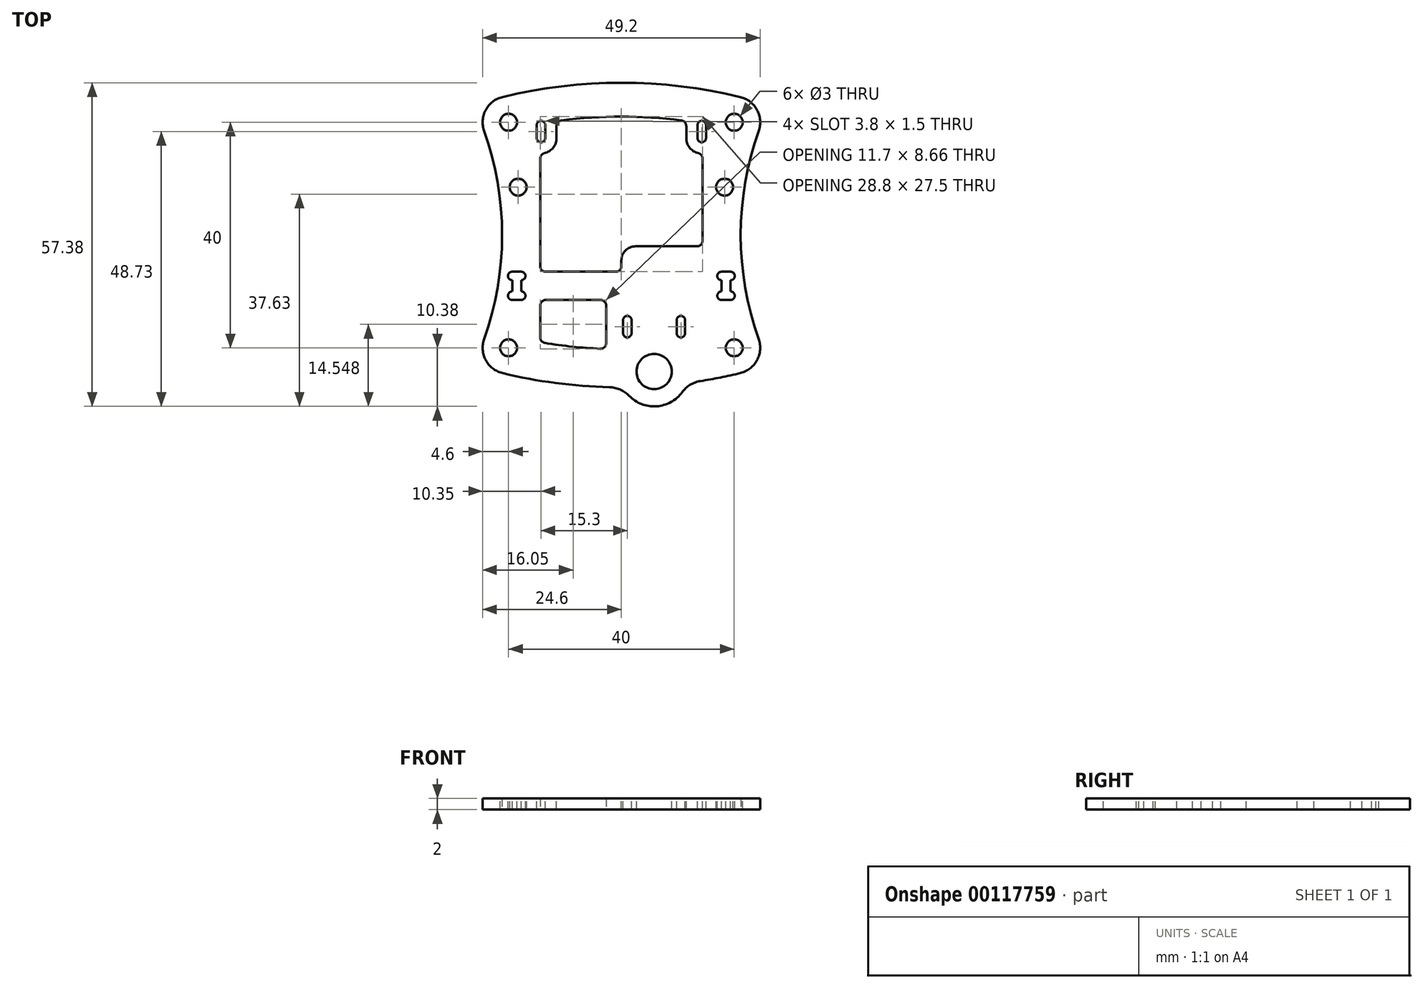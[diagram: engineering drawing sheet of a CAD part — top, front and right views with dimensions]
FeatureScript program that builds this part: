
annotation { "Feature Type Name" : "Feature", "Feature Type Description" : "" }
export const myFeature = defineFeature(function(context is Context, id is Id, definition is map)
    precondition{}
    {
        {
            var Q0;
            Q0=qCreatedBy(makeId("Top.planeOp"),FACE);
            var sketch = newSketch(context, id + "F0", { "sketchPlane" : qUnion([Q0])});
            skArc(sketch, "E0", {"start": v(-24.33, 18.46) * mm, "mid": v(-21.95, 9.37) * mm, "end": v(-21.15, 0) * mm});
            skLineSegment(sketch, "E1", {"start": v(-20, 0) * mm, "end": v(0, 0) * mm, "construction": true});
            skLineSegment(sketch, "E2", {"start": v(0, 0) * mm, "end": v(0, 20) * mm, "construction": true});
            skArc(sketch, "E3", {"start": v(-24.33, 18.46) * mm, "mid": v(-23.25, 23.25) * mm, "end": v(-18.46, 24.33) * mm});
            skArc(sketch, "E4", {"start": v(-18.46, 24.33) * mm, "mid": v(-9.37, 21.95) * mm, "end": v(0, 21.15) * mm});
            skPoint(sketch, "E4.centerSnap0", {"position": v(0, 10) * mm});
            skArc(sketch, "E5.MirrorCS", {"start": v(24.33, 18.46) * mm, "mid": v(23.25, 23.25) * mm, "end": v(18.46, 24.33) * mm});
            skArc(sketch, "E6.MirrorCS", {"start": v(24.33, 18.46) * mm, "mid": v(21.95, 9.37) * mm, "end": v(21.15, 0) * mm});
            skArc(sketch, "E7.MirrorCS", {"start": v(18.46, 24.33) * mm, "mid": v(9.37, 21.95) * mm, "end": v(0, 21.15) * mm});
            skPoint(sketch, "E8", {"position": v(-24.6, 20) * mm});
            skArc(sketch, "E9.MirrorCS", {"start": v(-24.33, -18.46) * mm, "mid": v(-21.95, -9.37) * mm, "end": v(-21.15, 0) * mm});
            skArc(sketch, "E10.MirrorCS", {"start": v(-24.33, -18.46) * mm, "mid": v(-23.25, -23.25) * mm, "end": v(-18.46, -24.33) * mm});
            skArc(sketch, "E11.MirrorCS", {"start": v(-18.46, -24.33) * mm, "mid": v(-9.37, -21.95) * mm, "end": v(0, -21.15) * mm});
            skArc(sketch, "E12.MirrorCS", {"start": v(24.33, -18.46) * mm, "mid": v(21.95, -9.37) * mm, "end": v(21.15, 0) * mm});
            skArc(sketch, "E13.MirrorCS", {"start": v(24.33, -18.46) * mm, "mid": v(23.25, -23.25) * mm, "end": v(18.46, -24.33) * mm});
            skArc(sketch, "E14.MirrorCS", {"start": v(18.46, -24.33) * mm, "mid": v(9.37, -21.95) * mm, "end": v(0, -21.15) * mm});
            skPoint(sketch, "E15.MirrorP", {"position": v(-24.6, -20) * mm});
            skSolve(sketch);
        }
        {
            var Q0;
            Q0 = qSketchRegion(id + "F0", true);
            extrude(context, id + "F1", {"entities" : qUnion([Q0]), "depth" : 2 * mm});
        }
        {
            var Q0;
            Q0=makeQuery(id+"F1.opExtrude","CAP_FACE",FACE,{"disambiguationData":[OSD([sQuery(id+"F0.wireOp",EDGE,"E0"),sQuery(id+"F0.wireOp",EDGE,"E3"),sQuery(id+"F0.wireOp",EDGE,"E4"),sQuery(id+"F0.wireOp",EDGE,"E5.MirrorCS"),sQuery(id+"F0.wireOp",EDGE,"E6.MirrorCS"),sQuery(id+"F0.wireOp",EDGE,"E7.MirrorCS"),sQuery(id+"F0.wireOp",EDGE,"E9.MirrorCS"),sQuery(id+"F0.wireOp",EDGE,"E11.MirrorCS"),sQuery(id+"F0.wireOp",EDGE,"E12.MirrorCS"),sQuery(id+"F0.wireOp",EDGE,"E13.MirrorCS"),sQuery(id+"F0.wireOp",EDGE,"E14.MirrorCS"),sQuery(id+"F0.wireOp",EDGE,"E10.MirrorCS")])],"isStart":false});
            var sketch = newSketch(context, id + "F2", { "sketchPlane" : qUnion([Q0])});
            skLineSegment(sketch, "E16", {"start": v(0, 0) * mm, "end": v(0, -65.87) * mm, "construction": true});
            skArc(sketch, "E17", {"start": v(-19.35, -6.5) * mm, "mid": v(-20.1, -7.25) * mm, "end": v(-19.35, -8) * mm});
            skLineSegment(sketch, "E18", {"start": v(-18.55, -6.5) * mm, "end": v(-18.55, -9) * mm, "construction": true});
            skLineSegment(sketch, "E19", {"start": v(-18.55, -9) * mm, "end": v(-19.35, -9) * mm, "construction": true});
            skLineSegment(sketch, "E20", {"start": v(-19.35, -6.5) * mm, "end": v(-18.55, -6.5) * mm});
            skLineSegment(sketch, "E21", {"start": v(-19.35, -8) * mm, "end": v(-19.35, -9) * mm});
            skLineSegment(sketch, "E22.MirrorCS", {"start": v(-19.35, -11.5) * mm, "end": v(-18.55, -11.5) * mm});
            skArc(sketch, "E23.MirrorCS", {"start": v(-19.35, -11.5) * mm, "mid": v(-20.1, -10.75) * mm, "end": v(-19.35, -10) * mm});
            skLineSegment(sketch, "E24.MirrorCS", {"start": v(-19.35, -10) * mm, "end": v(-19.35, -9) * mm});
            skArc(sketch, "E25.MirrorCS", {"start": v(-17.75, -11.5) * mm, "mid": v(-17, -10.75) * mm, "end": v(-17.75, -10) * mm});
            skLineSegment(sketch, "E26.MirrorCS", {"start": v(-17.75, -10) * mm, "end": v(-17.75, -9) * mm});
            skLineSegment(sketch, "E27.MirrorCS", {"start": v(-17.75, -8) * mm, "end": v(-17.75, -9) * mm});
            skArc(sketch, "E28.MirrorCS", {"start": v(-17.75, -6.5) * mm, "mid": v(-17, -7.25) * mm, "end": v(-17.75, -8) * mm});
            skLineSegment(sketch, "E29.MirrorCS", {"start": v(-17.75, -6.5) * mm, "end": v(-18.55, -6.5) * mm});
            skLineSegment(sketch, "E30.MirrorCS", {"start": v(-17.75, -11.5) * mm, "end": v(-18.55, -11.5) * mm});
            skArc(sketch, "E31.MirrorCS", {"start": v(19.35, -11.5) * mm, "mid": v(20.1, -10.75) * mm, "end": v(19.35, -10) * mm});
            skLineSegment(sketch, "E32.MirrorCS", {"start": v(19.35, -10) * mm, "end": v(19.35, -9) * mm});
            skLineSegment(sketch, "E33.MirrorCS", {"start": v(17.75, -8) * mm, "end": v(17.75, -9) * mm});
            skLineSegment(sketch, "E34.MirrorCS", {"start": v(19.35, -8) * mm, "end": v(19.35, -9) * mm});
            skArc(sketch, "E35.MirrorCS", {"start": v(17.75, -6.5) * mm, "mid": v(17, -7.25) * mm, "end": v(17.75, -8) * mm});
            skLineSegment(sketch, "E36.MirrorCS", {"start": v(17.75, -6.5) * mm, "end": v(18.55, -6.5) * mm});
            skLineSegment(sketch, "E37.MirrorCS", {"start": v(19.35, -6.5) * mm, "end": v(18.55, -6.5) * mm});
            skArc(sketch, "E38.MirrorCS", {"start": v(19.35, -6.5) * mm, "mid": v(20.1, -7.25) * mm, "end": v(19.35, -8) * mm});
            skLineSegment(sketch, "E39.MirrorCS", {"start": v(17.75, -10) * mm, "end": v(17.75, -9) * mm});
            skArc(sketch, "E40.MirrorCS", {"start": v(17.75, -11.5) * mm, "mid": v(17, -10.75) * mm, "end": v(17.75, -10) * mm});
            skLineSegment(sketch, "E41.MirrorCS", {"start": v(19.35, -11.5) * mm, "end": v(18.55, -11.5) * mm});
            skLineSegment(sketch, "E42.MirrorCS", {"start": v(17.75, -11.5) * mm, "end": v(18.55, -11.5) * mm});
            skSolve(sketch);
        }
        {
            var Q0;
            Q0 = qSketchRegion(id + "F2", true);
            extrude(context, id + "F3", {"entities" : qUnion([Q0]), "operationType" : NewBodyOperationType.REMOVE, "endBound" : BoundingType.THROUGH_ALL, "oppositeDirection" : true, "depth" : 25 * mm});
        }
        {
            var Q0;
            Q0=makeQuery(id+"F1.opExtrude","CAP_FACE",FACE,{"disambiguationData":[OSD([sQuery(id+"F0.wireOp",EDGE,"E0"),sQuery(id+"F0.wireOp",EDGE,"E3"),sQuery(id+"F0.wireOp",EDGE,"E4"),sQuery(id+"F0.wireOp",EDGE,"E5.MirrorCS"),sQuery(id+"F0.wireOp",EDGE,"E6.MirrorCS"),sQuery(id+"F0.wireOp",EDGE,"E7.MirrorCS"),sQuery(id+"F0.wireOp",EDGE,"E9.MirrorCS"),sQuery(id+"F0.wireOp",EDGE,"E11.MirrorCS"),sQuery(id+"F0.wireOp",EDGE,"E12.MirrorCS"),sQuery(id+"F0.wireOp",EDGE,"E13.MirrorCS"),sQuery(id+"F0.wireOp",EDGE,"E14.MirrorCS"),sQuery(id+"F0.wireOp",EDGE,"E10.MirrorCS")])],"isStart":false});
            var sketch = newSketch(context, id + "F4", { "sketchPlane" : qUnion([Q0])});
            skPoint(sketch, "E43", {"position": v(-20, 20) * mm});
            skPoint(sketch, "E44", {"position": v(20, 20) * mm});
            skPoint(sketch, "E45", {"position": v(20, -20) * mm});
            skPoint(sketch, "E46", {"position": v(-20, -20) * mm});
            skPoint(sketch, "E47", {"position": v(-18.3, 8.5) * mm});
            skPoint(sketch, "E48.MirrorP", {"position": v(18.3, 8.5) * mm});
            skSolve(sketch);
        }
        {
            var Q0;
            Q0=sQuery(id+"F4.wireOp",VERTEX,"E47");
            var Q1;
            Q1=sQuery(id+"F4.wireOp",VERTEX,"E43");
            var Q2;
            Q2=sQuery(id+"F4.wireOp",VERTEX,"E44");
            var Q3;
            Q3=sQuery(id+"F4.wireOp",VERTEX,"E48.MirrorP");
            var Q4;
            Q4=sQuery(id+"F4.wireOp",VERTEX,"E45");
            var Q5;
            Q5=sQuery(id+"F4.wireOp",VERTEX,"E46");
            var Q6;
            Q6=makeQuery(id+"F1.opExtrude","SWEPT_BODY",BODY,{"disambiguationData":[OSD([sQuery(id+"F0.wireOp",EDGE,"E0"),sQuery(id+"F0.wireOp",EDGE,"E3"),sQuery(id+"F0.wireOp",EDGE,"E4"),sQuery(id+"F0.wireOp",EDGE,"E5.MirrorCS"),sQuery(id+"F0.wireOp",EDGE,"E6.MirrorCS"),sQuery(id+"F0.wireOp",EDGE,"E7.MirrorCS"),sQuery(id+"F0.wireOp",EDGE,"E9.MirrorCS"),sQuery(id+"F0.wireOp",EDGE,"E11.MirrorCS"),sQuery(id+"F0.wireOp",EDGE,"E12.MirrorCS"),sQuery(id+"F0.wireOp",EDGE,"E13.MirrorCS"),sQuery(id+"F0.wireOp",EDGE,"E14.MirrorCS"),sQuery(id+"F0.wireOp",EDGE,"E10.MirrorCS")])]});
            hole(context, id + "F5", {"style" : HoleStyle.SIMPLE, "endStyle" : HoleEndStyle.THROUGH, "holeDiameter" : 3 * mm, "locations" : qUnion([Q0, Q1, Q2, Q3, Q4, Q5]), "scope" : qUnion([Q6]), "isTappedThrough" : true});
        }
        {
            var Q0;
            Q0=qCreatedBy(makeId("Top.planeOp"),FACE);
            var sketch = newSketch(context, id + "F6", { "sketchPlane" : qUnion([Q0])});
            skLineSegment(sketch, "E49", {"start": v(0, 0) * mm, "end": v(0, -30.33) * mm, "construction": true});
            skCircle(sketch, "E50", {"center": v(5.8, -24.2) * mm, "radius": 3.18 * mm});
            skLineSegment(sketch, "E51", {"start": v(-30.33, 18) * mm, "end": v(30.33, 18) * mm, "construction": true});
            skLineSegment(sketch, "E52", {"start": v(0, 0) * mm, "end": v(-30.33, 0) * mm, "construction": true});
            skLineSegment(sketch, "E53.bottom", {"start": v(-11, 25) * mm, "end": v(11, 25) * mm});
            skLineSegment(sketch, "E53.top", {"start": v(-11, -6) * mm, "end": v(11, -6) * mm});
            skLineSegment(sketch, "E53.left", {"start": v(-11, 25) * mm, "end": v(-11, -6) * mm});
            skLineSegment(sketch, "E53.right", {"start": v(11, 25) * mm, "end": v(11, -6) * mm});
            skLineSegment(sketch, "E54.bottom", {"start": v(-4, 25) * mm, "end": v(5.6, 25) * mm});
            skLineSegment(sketch, "E54.top", {"start": v(-4, 20) * mm, "end": v(5.6, 20) * mm});
            skLineSegment(sketch, "E54.left", {"start": v(-4, 25) * mm, "end": v(-4, 20) * mm});
            skLineSegment(sketch, "E54.right", {"start": v(5.6, 25) * mm, "end": v(5.6, 20) * mm});
            skLineSegment(sketch, "E55.bottom", {"start": v(1.25, -6) * mm, "end": v(10.35, -6) * mm});
            skLineSegment(sketch, "E55.top", {"start": v(1.25, -21.02) * mm, "end": v(10.35, -21.02) * mm});
            skLineSegment(sketch, "E55.left", {"start": v(1.25, -6) * mm, "end": v(1.25, -21.02) * mm});
            skLineSegment(sketch, "E55.right", {"start": v(10.35, -6) * mm, "end": v(10.35, -21.02) * mm});
            skLineSegment(sketch, "E56", {"start": v(5.8, -24.2) * mm, "end": v(5.8, -21.02) * mm, "construction": true});
            skPoint(sketch, "E56.endSnap0", {"position": v(5.8, -6) * mm});
            skLineSegment(sketch, "E57.bottom", {"start": v(-11, 0) * mm, "end": v(11, 0) * mm});
            skLineSegment(sketch, "E57.top", {"start": v(-11, 19.5) * mm, "end": v(11, 19.5) * mm});
            skLineSegment(sketch, "E57.left", {"start": v(-11, 0) * mm, "end": v(-11, 19.5) * mm});
            skLineSegment(sketch, "E57.right", {"start": v(11, 0) * mm, "end": v(11, 19.5) * mm});
            skSolve(sketch);
        }
        {
            var Q0;
            Q0=qCreatedBy(makeId("Top.planeOp"),FACE);
            var sketch = newSketch(context, id + "F7", { "sketchPlane" : qUnion([Q0])});
            skLineSegment(sketch, "E58", {"start": v(0, 0) * mm, "end": v(0, 27) * mm, "construction": true});
            skArc(sketch, "E59", {"start": v(0, 27) * mm, "mid": v(-10.62, 26.37) * mm, "end": v(-21.09, 24.47) * mm});
            skLineSegment(sketch, "E60", {"start": v(0, 27) * mm, "end": v(-20.39, 27) * mm, "construction": true});
            skArc(sketch, "E61", {"start": v(-21.09, 24.47) * mm, "mid": v(-19.76, 24.6) * mm, "end": v(-18.46, 24.33) * mm});
            skArc(sketch, "E62", {"start": v(-18.46, 24.33) * mm, "mid": v(-9.37, 21.95) * mm, "end": v(0, 21.15) * mm});
            skArc(sketch, "E63.MirrorCS", {"start": v(18.46, 24.33) * mm, "mid": v(9.37, 21.95) * mm, "end": v(0, 21.15) * mm});
            skArc(sketch, "E64.MirrorCS", {"start": v(21.09, 24.47) * mm, "mid": v(19.76, 24.6) * mm, "end": v(18.46, 24.33) * mm});
            skArc(sketch, "E65.MirrorCS", {"start": v(0, 27) * mm, "mid": v(10.62, 26.37) * mm, "end": v(21.09, 24.47) * mm});
            skSolve(sketch);
        }
        {
            var Q0;
            Q0 = qSketchRegion(id + "F7", true);
            var Q1;
            Q1=makeQuery(id+"F1.opExtrude","CAP_FACE",FACE,{"disambiguationData":[OSD([sQuery(id+"F0.wireOp",EDGE,"E0"),sQuery(id+"F0.wireOp",EDGE,"E3"),sQuery(id+"F0.wireOp",EDGE,"E4"),sQuery(id+"F0.wireOp",EDGE,"E5.MirrorCS"),sQuery(id+"F0.wireOp",EDGE,"E6.MirrorCS"),sQuery(id+"F0.wireOp",EDGE,"E7.MirrorCS"),sQuery(id+"F0.wireOp",EDGE,"E9.MirrorCS"),sQuery(id+"F0.wireOp",EDGE,"E11.MirrorCS"),sQuery(id+"F0.wireOp",EDGE,"E12.MirrorCS"),sQuery(id+"F0.wireOp",EDGE,"E13.MirrorCS"),sQuery(id+"F0.wireOp",EDGE,"E14.MirrorCS"),sQuery(id+"F0.wireOp",EDGE,"E10.MirrorCS")])],"isStart":false});
            extrude(context, id + "F8", {"entities" : qUnion([Q0]), "operationType" : NewBodyOperationType.ADD, "endBound" : BoundingType.UP_TO_SURFACE, "endBoundEntityFace" : qUnion([Q1]), "depth" : 25 * mm});
        }
        {
            var Q0;
            Q0=qCreatedBy(makeId("Top.planeOp"),FACE);
            var sketch = newSketch(context, id + "F9", { "sketchPlane" : qUnion([Q0])});
            skLineSegment(sketch, "E66", {"start": v(0, 0) * mm, "end": v(30.86, 0) * mm, "construction": true});
            skArc(sketch, "E67", {"start": v(21.09, -24.47) * mm, "mid": v(16.38, -25.48) * mm, "end": v(11.63, -26.24) * mm});
            skLineSegment(sketch, "E68", {"start": v(0, -27) * mm, "end": v(0, 0) * mm, "construction": true});
            skLineSegment(sketch, "E69", {"start": v(0, -27) * mm, "end": v(19.98, -27) * mm, "construction": true});
            skArc(sketch, "E70.MirrorCS", {"start": v(-21.09, -24.47) * mm, "mid": v(-10.47, -26.38) * mm, "end": v(0.3, -27) * mm});
            skArc(sketch, "E71", {"start": v(0.3, -27) * mm, "mid": v(6.21, -30.36) * mm, "end": v(11.63, -26.24) * mm});
            skArc(sketch, "E72", {"start": v(0, -21.15) * mm, "mid": v(9.37, -21.95) * mm, "end": v(18.46, -24.33) * mm});
            skArc(sketch, "E73", {"start": v(21.09, -24.47) * mm, "mid": v(19.76, -24.6) * mm, "end": v(18.46, -24.33) * mm});
            skArc(sketch, "E74.MirrorCS", {"start": v(-21.09, -24.47) * mm, "mid": v(-19.76, -24.6) * mm, "end": v(-18.46, -24.33) * mm});
            skArc(sketch, "E75.MirrorCS", {"start": v(0, -21.15) * mm, "mid": v(-9.37, -21.95) * mm, "end": v(-18.46, -24.33) * mm});
            skPoint(sketch, "E76.orphan", {"position": v(0, -27) * mm});
            skSolve(sketch);
        }
        {
            var Q0;
            Q0 = qSketchRegion(id + "F9", true);
            var Q1;
            {var subQ0=sQuery(id+"F0.wireOp",EDGE,"E10.MirrorCS");var subQ1=sQuery(id+"F0.wireOp",EDGE,"E14.MirrorCS");var subQ2=sQuery(id+"F0.wireOp",EDGE,"E13.MirrorCS");var subQ3=sQuery(id+"F0.wireOp",EDGE,"E12.MirrorCS");var subQ4=sQuery(id+"F0.wireOp",EDGE,"E11.MirrorCS");var subQ5=sQuery(id+"F0.wireOp",EDGE,"E9.MirrorCS");var subQ6=sQuery(id+"F0.wireOp",EDGE,"E7.MirrorCS");var subQ7=sQuery(id+"F0.wireOp",EDGE,"E6.MirrorCS");var subQ8=sQuery(id+"F0.wireOp",EDGE,"E5.MirrorCS");var subQ9=sQuery(id+"F0.wireOp",EDGE,"E4");var subQ10=sQuery(id+"F0.wireOp",EDGE,"E3");var subQ11=sQuery(id+"F0.wireOp",EDGE,"E0");Q1=makeQuery(id+"F8.boolean.opBoolean","MERGE",FACE,{"derivedFrom":[makeQuery(id+"F1.opExtrude","CAP_FACE",FACE,{"disambiguationData":[OSD([subQ11,subQ10,subQ9,subQ8,subQ7,subQ6,subQ5,subQ4,subQ3,subQ2,subQ1,subQ0])],"isStart":false}),makeQuery(id+"F8.opExtrude","CAP_FACE",FACE,{"disambiguationData":[OSD([subQ11,subQ10,subQ9,subQ8,subQ7,subQ6,subQ5,subQ4,subQ3,subQ2,subQ1,subQ0])],"isStart":false})]});}
            extrude(context, id + "F10", {"entities" : qUnion([Q0]), "operationType" : NewBodyOperationType.ADD, "endBound" : BoundingType.UP_TO_SURFACE, "endBoundEntityFace" : qUnion([Q1]), "depth" : 25 * mm});
        }
        {
            var Q0;
            Q0=makeQuery(id+"F10.opExtrude","SWEPT_EDGE",EDGE,{"disambiguationData":[OSD([sQuery(id+"F9.wireOp",EDGE,"E70.MirrorCS"),sQuery(id+"F9.wireOp",EDGE,"E71")])]});
            var Q1;
            Q1=makeQuery(id+"F10.opExtrude","SWEPT_EDGE",EDGE,{"disambiguationData":[OSD([sQuery(id+"F9.wireOp",EDGE,"E67"),sQuery(id+"F9.wireOp",EDGE,"E71")])]});
            fillet(context, id + "F11", {"entities" : qUnion([Q0, Q1]), "radius" : 5 * mm, "tangentPropagation" : true, "allowEdgeOverflow" : false});
        }
        {
            var Q0;
            {var subQ0=sQuery(id+"F0.wireOp",EDGE,"E10.MirrorCS");var subQ1=sQuery(id+"F0.wireOp",EDGE,"E14.MirrorCS");var subQ2=sQuery(id+"F0.wireOp",EDGE,"E13.MirrorCS");var subQ3=sQuery(id+"F0.wireOp",EDGE,"E12.MirrorCS");var subQ4=sQuery(id+"F0.wireOp",EDGE,"E11.MirrorCS");var subQ5=sQuery(id+"F0.wireOp",EDGE,"E9.MirrorCS");var subQ6=sQuery(id+"F0.wireOp",EDGE,"E7.MirrorCS");var subQ7=sQuery(id+"F0.wireOp",EDGE,"E6.MirrorCS");var subQ8=sQuery(id+"F0.wireOp",EDGE,"E5.MirrorCS");var subQ9=sQuery(id+"F0.wireOp",EDGE,"E4");var subQ10=sQuery(id+"F0.wireOp",EDGE,"E3");var subQ11=sQuery(id+"F0.wireOp",EDGE,"E0");Q0=makeQuery(id+"F10.boolean.opBoolean","MERGE",FACE,{"derivedFrom":[makeQuery(id+"F8.boolean.opBoolean","MERGE",FACE,{"derivedFrom":[makeQuery(id+"F1.opExtrude","CAP_FACE",FACE,{"disambiguationData":[OSD([subQ11,subQ10,subQ9,subQ8,subQ7,subQ6,subQ5,subQ4,subQ3,subQ2,subQ1,subQ0])],"isStart":false}),makeQuery(id+"F8.opExtrude","CAP_FACE",FACE,{"disambiguationData":[OSD([subQ11,subQ10,subQ9,subQ8,subQ7,subQ6,subQ5,subQ4,subQ3,subQ2,subQ1,subQ0])],"isStart":false})]}),makeQuery(id+"F10.opExtrude","CAP_FACE",FACE,{"disambiguationData":[OSD([subQ11,subQ10,subQ9,subQ8,subQ7,subQ6,subQ5,subQ4,subQ3,subQ2,subQ1,subQ0])],"isStart":false})]});}
            var sketch = newSketch(context, id + "F12", { "sketchPlane" : qUnion([Q0])});
            skLineSegment(sketch, "E77", {"start": v(5.8, 3.6) * mm, "end": v(5.8, -24.2) * mm, "construction": true});
            skLineSegment(sketch, "E78", {"start": v(0, 0) * mm, "end": v(0, 29.06) * mm, "construction": true});
            skPoint(sketch, "E78.endSnap0", {"position": v(0, 27) * mm});
            skLineSegment(sketch, "E79.left", {"start": v(9.8, -15.1) * mm, "end": v(9.8, -17.4) * mm});
            skLineSegment(sketch, "E79.right", {"start": v(11.3, -15.1) * mm, "end": v(11.3, -17.4) * mm});
            skArc(sketch, "E80", {"start": v(11.3, -15.1) * mm, "mid": v(10.55, -14.35) * mm, "end": v(9.8, -15.1) * mm});
            skArc(sketch, "E81", {"start": v(9.8, -17.4) * mm, "mid": v(10.55, -18.15) * mm, "end": v(11.3, -17.4) * mm});
            skLineSegment(sketch, "E82", {"start": v(10.55, -17.4) * mm, "end": v(10.55, -15.1) * mm});
            skPoint(sketch, "E83", {"position": v(10.55, -16.25) * mm});
            skLineSegment(sketch, "E84.MirrorCS", {"start": v(0.3, -15.1) * mm, "end": v(0.3, -17.4) * mm});
            skArc(sketch, "E85.MirrorCS", {"start": v(0.3, -15.1) * mm, "mid": v(1.05, -14.35) * mm, "end": v(1.8, -15.1) * mm});
            skLineSegment(sketch, "E86.MirrorCS", {"start": v(1.8, -15.1) * mm, "end": v(1.8, -17.4) * mm});
            skArc(sketch, "E87.MirrorCS", {"start": v(1.8, -17.4) * mm, "mid": v(1.05, -18.15) * mm, "end": v(0.3, -17.4) * mm});
            skLineSegment(sketch, "E88.left", {"start": v(13.5, 19.5) * mm, "end": v(13.5, 17.2) * mm});
            skLineSegment(sketch, "E88.right", {"start": v(15, 19.5) * mm, "end": v(15, 17.2) * mm});
            skArc(sketch, "E89", {"start": v(15, 19.5) * mm, "mid": v(14.25, 20.25) * mm, "end": v(13.5, 19.5) * mm});
            skArc(sketch, "E90", {"start": v(13.5, 17.2) * mm, "mid": v(14.25, 16.45) * mm, "end": v(15, 17.2) * mm});
            skArc(sketch, "E91.MirrorCS", {"start": v(-15, 19.5) * mm, "mid": v(-14.25, 20.25) * mm, "end": v(-13.5, 19.5) * mm});
            skLineSegment(sketch, "E92.MirrorCS", {"start": v(-13.5, 19.5) * mm, "end": v(-13.5, 17.2) * mm});
            skLineSegment(sketch, "E93.MirrorCS", {"start": v(-15, 19.5) * mm, "end": v(-15, 17.2) * mm});
            skArc(sketch, "E94.MirrorCS", {"start": v(-13.5, 17.2) * mm, "mid": v(-14.25, 16.45) * mm, "end": v(-15, 17.2) * mm});
            skSolve(sketch);
        }
        {
            var Q0;
            Q0 = qSketchRegion(id + "F12", true);
            extrude(context, id + "F13", {"entities" : qUnion([Q0]), "operationType" : NewBodyOperationType.REMOVE, "endBound" : BoundingType.THROUGH_ALL, "oppositeDirection" : true, "depth" : 25 * mm});
        }
        {
            var Q0;
            {var subQ0=sQuery(id+"F0.wireOp",EDGE,"E10.MirrorCS");var subQ1=sQuery(id+"F0.wireOp",EDGE,"E14.MirrorCS");var subQ2=sQuery(id+"F0.wireOp",EDGE,"E13.MirrorCS");var subQ3=sQuery(id+"F0.wireOp",EDGE,"E12.MirrorCS");var subQ4=sQuery(id+"F0.wireOp",EDGE,"E11.MirrorCS");var subQ5=sQuery(id+"F0.wireOp",EDGE,"E9.MirrorCS");var subQ6=sQuery(id+"F0.wireOp",EDGE,"E7.MirrorCS");var subQ7=sQuery(id+"F0.wireOp",EDGE,"E6.MirrorCS");var subQ8=sQuery(id+"F0.wireOp",EDGE,"E5.MirrorCS");var subQ9=sQuery(id+"F0.wireOp",EDGE,"E4");var subQ10=sQuery(id+"F0.wireOp",EDGE,"E3");var subQ11=sQuery(id+"F0.wireOp",EDGE,"E0");Q0=makeQuery(id+"F10.boolean.opBoolean","MERGE",FACE,{"derivedFrom":[makeQuery(id+"F8.boolean.opBoolean","MERGE",FACE,{"derivedFrom":[makeQuery(id+"F1.opExtrude","CAP_FACE",FACE,{"disambiguationData":[OSD([subQ11,subQ10,subQ9,subQ8,subQ7,subQ6,subQ5,subQ4,subQ3,subQ2,subQ1,subQ0])],"isStart":false}),makeQuery(id+"F8.opExtrude","CAP_FACE",FACE,{"disambiguationData":[OSD([subQ11,subQ10,subQ9,subQ8,subQ7,subQ6,subQ5,subQ4,subQ3,subQ2,subQ1,subQ0])],"isStart":false})]}),makeQuery(id+"F10.opExtrude","CAP_FACE",FACE,{"disambiguationData":[OSD([subQ11,subQ10,subQ9,subQ8,subQ7,subQ6,subQ5,subQ4,subQ3,subQ2,subQ1,subQ0])],"isStart":false})]});}
            var sketch = newSketch(context, id + "F14", { "sketchPlane" : qUnion([Q0])});
            skCircle(sketch, "E95", {"center": v(5.8, -24.2) * mm, "radius": 3.12 * mm});
            skSolve(sketch);
        }
        {
            var Q0;
            Q0 = qSketchRegion(id + "F14", true);
            extrude(context, id + "F15", {"entities" : qUnion([Q0]), "operationType" : NewBodyOperationType.REMOVE, "endBound" : BoundingType.THROUGH_ALL, "oppositeDirection" : true, "depth" : 25 * mm});
        }
        {
            var Q0;
            {var subQ0=sQuery(id+"F0.wireOp",EDGE,"E10.MirrorCS");var subQ1=sQuery(id+"F0.wireOp",EDGE,"E14.MirrorCS");var subQ2=sQuery(id+"F0.wireOp",EDGE,"E13.MirrorCS");var subQ3=sQuery(id+"F0.wireOp",EDGE,"E12.MirrorCS");var subQ4=sQuery(id+"F0.wireOp",EDGE,"E11.MirrorCS");var subQ5=sQuery(id+"F0.wireOp",EDGE,"E9.MirrorCS");var subQ6=sQuery(id+"F0.wireOp",EDGE,"E7.MirrorCS");var subQ7=sQuery(id+"F0.wireOp",EDGE,"E6.MirrorCS");var subQ8=sQuery(id+"F0.wireOp",EDGE,"E5.MirrorCS");var subQ9=sQuery(id+"F0.wireOp",EDGE,"E4");var subQ10=sQuery(id+"F0.wireOp",EDGE,"E3");var subQ11=sQuery(id+"F0.wireOp",EDGE,"E0");Q0=makeQuery(id+"F10.boolean.opBoolean","MERGE",FACE,{"derivedFrom":[makeQuery(id+"F8.boolean.opBoolean","MERGE",FACE,{"derivedFrom":[makeQuery(id+"F1.opExtrude","CAP_FACE",FACE,{"disambiguationData":[OSD([subQ11,subQ10,subQ9,subQ8,subQ7,subQ6,subQ5,subQ4,subQ3,subQ2,subQ1,subQ0])],"isStart":false}),makeQuery(id+"F8.opExtrude","CAP_FACE",FACE,{"disambiguationData":[OSD([subQ11,subQ10,subQ9,subQ8,subQ7,subQ6,subQ5,subQ4,subQ3,subQ2,subQ1,subQ0])],"isStart":false})]}),makeQuery(id+"F10.opExtrude","CAP_FACE",FACE,{"disambiguationData":[OSD([subQ11,subQ10,subQ9,subQ8,subQ7,subQ6,subQ5,subQ4,subQ3,subQ2,subQ1,subQ0])],"isStart":false})]});}
            var sketch = newSketch(context, id + "F16", { "sketchPlane" : qUnion([Q0])});
            skPoint(sketch, "E96", {"position": v(0, 27) * mm});
            skLineSegment(sketch, "E97", {"start": v(-14.4, 14.45) * mm, "end": v(-14.4, -6.5) * mm});
            skPoint(sketch, "E98", {"position": v(-21.15, 0) * mm});
            skLineSegment(sketch, "E99", {"start": v(14.4, 14.45) * mm, "end": v(14.4, -2) * mm});
            skPoint(sketch, "E100", {"position": v(21.15, 0) * mm});
            skArc(sketch, "E101", {"start": v(-11.5, 20.2) * mm, "mid": v(0, 21) * mm, "end": v(11.5, 20.2) * mm});
            skLineSegment(sketch, "E102", {"start": v(-2.7, -20.2) * mm, "end": v(-2.7, -11.5) * mm});
            skLineSegment(sketch, "E103", {"start": v(0, -2) * mm, "end": v(14.4, -2) * mm});
            skLineSegment(sketch, "E104", {"start": v(-11.5, 17.2) * mm, "end": v(-11.5, 20.2) * mm});
            skPoint(sketch, "E105", {"position": v(-14.25, 17.2) * mm});
            skArc(sketch, "E106", {"start": v(-11.5, 17.2) * mm, "mid": v(-12.36, 15.2) * mm, "end": v(-14.4, 14.45) * mm});
            skLineSegment(sketch, "E107", {"start": v(0, 0) * mm, "end": v(0, 21) * mm, "construction": true});
            skPoint(sketch, "E108", {"position": v(-14.25, 16.45) * mm});
            skArc(sketch, "E109.MirrorCS", {"start": v(11.5, 17.2) * mm, "mid": v(12.36, 15.2) * mm, "end": v(14.4, 14.45) * mm});
            skLineSegment(sketch, "E110.MirrorCS", {"start": v(11.5, 17.2) * mm, "end": v(11.5, 20.2) * mm});
            skArc(sketch, "E111", {"start": v(-14.4, -18.98) * mm, "mid": v(-8.57, -19.8) * mm, "end": v(-2.7, -20.2) * mm});
            skLineSegment(sketch, "E112", {"start": v(-2.7, -11.5) * mm, "end": v(-14.4, -11.5) * mm});
            skLineSegment(sketch, "E113", {"start": v(-14.4, -6.5) * mm, "end": v(0, -6.5) * mm});
            skLineSegment(sketch, "E114.trimOffspring", {"start": v(0, -6.5) * mm, "end": v(0, -2) * mm});
            skLineSegment(sketch, "E115.trimOffspring", {"start": v(-14.4, -11.5) * mm, "end": v(-14.4, -18.98) * mm});
            skLineSegment(sketch, "E116", {"start": v(5.8, -24.2) * mm, "end": v(5.8, -21.07) * mm, "construction": true});
            skSolve(sketch);
        }
        {
            var Q0;
            Q0 = qSketchRegion(id + "F16", true);
            extrude(context, id + "F17", {"entities" : qUnion([Q0]), "operationType" : NewBodyOperationType.REMOVE, "endBound" : BoundingType.THROUGH_ALL, "oppositeDirection" : true, "depth" : 25 * mm});
        }
        {
            var Q0;
            Q0=makeQuery(id+"F17.boolean.opBoolean","COPY",EDGE,{"derivedFrom":makeQuery(id+"F17.opExtrude","SWEPT_EDGE",EDGE,{"disambiguationData":[OSD([sQuery(id+"F16.wireOp",EDGE,"E102"),sQuery(id+"F16.wireOp",EDGE,"E112")])]})});
            var Q1;
            Q1=makeQuery(id+"F17.boolean.opBoolean","COPY",EDGE,{"derivedFrom":makeQuery(id+"F17.opExtrude","SWEPT_EDGE",EDGE,{"disambiguationData":[OSD([sQuery(id+"F16.wireOp",EDGE,"w48rfDKU-Ewvb-xwgp-HWHa-MmorG8pKUdSB.bottom"),sQuery(id+"F16.wireOp",EDGE,"w48rfDKU-Ewvb-xwgp-HWHa-MmorG8pKUdSB.right")])]})});
            var Q2;
            Q2=makeQuery(id+"F17.boolean.opBoolean","COPY",EDGE,{"derivedFrom":makeQuery(id+"F17.opExtrude","SWEPT_EDGE",EDGE,{"disambiguationData":[OSD([sQuery(id+"F16.wireOp",EDGE,"E112"),sQuery(id+"F16.wireOp",EDGE,"E115.trimOffspring")])]})});
            var Q3;
            Q3=makeQuery(id+"F17.boolean.opBoolean","COPY",EDGE,{"derivedFrom":makeQuery(id+"F17.opExtrude","SWEPT_EDGE",EDGE,{"disambiguationData":[OSD([sQuery(id+"F16.wireOp",EDGE,"E111"),sQuery(id+"F16.wireOp",EDGE,"E115.trimOffspring")])]})});
            var Q4;
            Q4=makeQuery(id+"F17.boolean.opBoolean","COPY",EDGE,{"derivedFrom":makeQuery(id+"F17.opExtrude","SWEPT_EDGE",EDGE,{"disambiguationData":[OSD([sQuery(id+"F16.wireOp",EDGE,"w48rfDKU-Ewvb-xwgp-HWHa-MmorG8pKUdSB.top"),sQuery(id+"F16.wireOp",EDGE,"w48rfDKU-Ewvb-xwgp-HWHa-MmorG8pKUdSB.left")])]})});
            var Q5;
            Q5=makeQuery(id+"F17.boolean.opBoolean","COPY",EDGE,{"derivedFrom":makeQuery(id+"F17.opExtrude","SWEPT_EDGE",EDGE,{"disambiguationData":[OSD([sQuery(id+"F16.wireOp",EDGE,"w48rfDKU-Ewvb-xwgp-HWHa-MmorG8pKUdSB.top"),sQuery(id+"F16.wireOp",EDGE,"w48rfDKU-Ewvb-xwgp-HWHa-MmorG8pKUdSB.right")])]})});
            var Q6;
            Q6=makeQuery(id+"F17.boolean.opBoolean","COPY",EDGE,{"derivedFrom":makeQuery(id+"F17.opExtrude","SWEPT_EDGE",EDGE,{"disambiguationData":[OSD([sQuery(id+"F16.wireOp",EDGE,"E102"),sQuery(id+"F16.wireOp",EDGE,"E111")])]})});
            var Q7;
            Q7=makeQuery(id+"F17.boolean.opBoolean","COPY",EDGE,{"derivedFrom":makeQuery(id+"F17.opExtrude","SWEPT_EDGE",EDGE,{"disambiguationData":[OSD([sQuery(id+"F16.wireOp",EDGE,"w48rfDKU-Ewvb-xwgp-HWHa-MmorG8pKUdSB.bottom"),sQuery(id+"F16.wireOp",EDGE,"w48rfDKU-Ewvb-xwgp-HWHa-MmorG8pKUdSB.left")])]})});
            var Q8;
            Q8=makeQuery(id+"F17.boolean.opBoolean","COPY",EDGE,{"derivedFrom":makeQuery(id+"F17.opExtrude","SWEPT_EDGE",EDGE,{"disambiguationData":[OSD([sQuery(id+"F16.wireOp",EDGE,"E101"),sQuery(id+"F16.wireOp",EDGE,"E110.MirrorCS")])]})});
            var Q9;
            Q9=makeQuery(id+"F17.boolean.opBoolean","COPY",EDGE,{"derivedFrom":makeQuery(id+"F17.opExtrude","SWEPT_EDGE",EDGE,{"disambiguationData":[OSD([sQuery(id+"F16.wireOp",EDGE,"E99"),sQuery(id+"F16.wireOp",EDGE,"242761ee-4380-49e1-bb36-9e82733fe9be0.MirrorCS")])]})});
            var Q10;
            Q10=makeQuery(id+"F17.boolean.opBoolean","COPY",EDGE,{"derivedFrom":makeQuery(id+"F17.opExtrude","SWEPT_EDGE",EDGE,{"disambiguationData":[OSD([sQuery(id+"F16.wireOp",EDGE,"E97"),sQuery(id+"F16.wireOp",EDGE,"YmPafNJ4-ENFf-a7qC-zsAM-NMp7mHHc5WH0")])]})});
            var Q11;
            Q11=makeQuery(id+"F17.boolean.opBoolean","COPY",EDGE,{"derivedFrom":makeQuery(id+"F17.opExtrude","SWEPT_EDGE",EDGE,{"disambiguationData":[OSD([sQuery(id+"F16.wireOp",EDGE,"E101"),sQuery(id+"F16.wireOp",EDGE,"E104")])]})});
            var Q12;
            Q12=makeQuery(id+"F17.boolean.opBoolean","COPY",EDGE,{"derivedFrom":makeQuery(id+"F17.opExtrude","SWEPT_EDGE",EDGE,{"disambiguationData":[OSD([sQuery(id+"F16.wireOp",EDGE,"E97"),sQuery(id+"F16.wireOp",EDGE,"E113")])]})});
            var Q13;
            Q13=makeQuery(id+"F17.boolean.opBoolean","COPY",EDGE,{"derivedFrom":makeQuery(id+"F17.opExtrude","SWEPT_EDGE",EDGE,{"disambiguationData":[OSD([sQuery(id+"F16.wireOp",EDGE,"E99"),sQuery(id+"F16.wireOp",EDGE,"E103")])]})});
            var Q14;
            Q14=makeQuery(id+"F17.boolean.opBoolean","COPY",EDGE,{"derivedFrom":makeQuery(id+"F17.opExtrude","SWEPT_EDGE",EDGE,{"disambiguationData":[OSD([sQuery(id+"F16.wireOp",EDGE,"E113"),sQuery(id+"F16.wireOp",EDGE,"E114.trimOffspring")])]})});
            fillet(context, id + "F18", {"entities" : qUnion([Q0, Q1, Q2, Q3, Q4, Q5, Q6, Q7, Q8, Q9, Q10, Q11, Q12, Q13, Q14]), "radius" : 1 * mm, "tangentPropagation" : true, "allowEdgeOverflow" : false});
        }
        {
            var Q0;
            Q0=makeQuery(id+"F17.boolean.opBoolean","COPY",EDGE,{"derivedFrom":makeQuery(id+"F17.opExtrude","SWEPT_EDGE",EDGE,{"disambiguationData":[OSD([sQuery(id+"F16.wireOp",EDGE,"E103"),sQuery(id+"F16.wireOp",EDGE,"E114.trimOffspring")])]})});
            fillet(context, id + "F19", {"entities" : qUnion([Q0]), "radius" : 2.5 * mm, "tangentPropagation" : true, "allowEdgeOverflow" : false});
        }
    });
